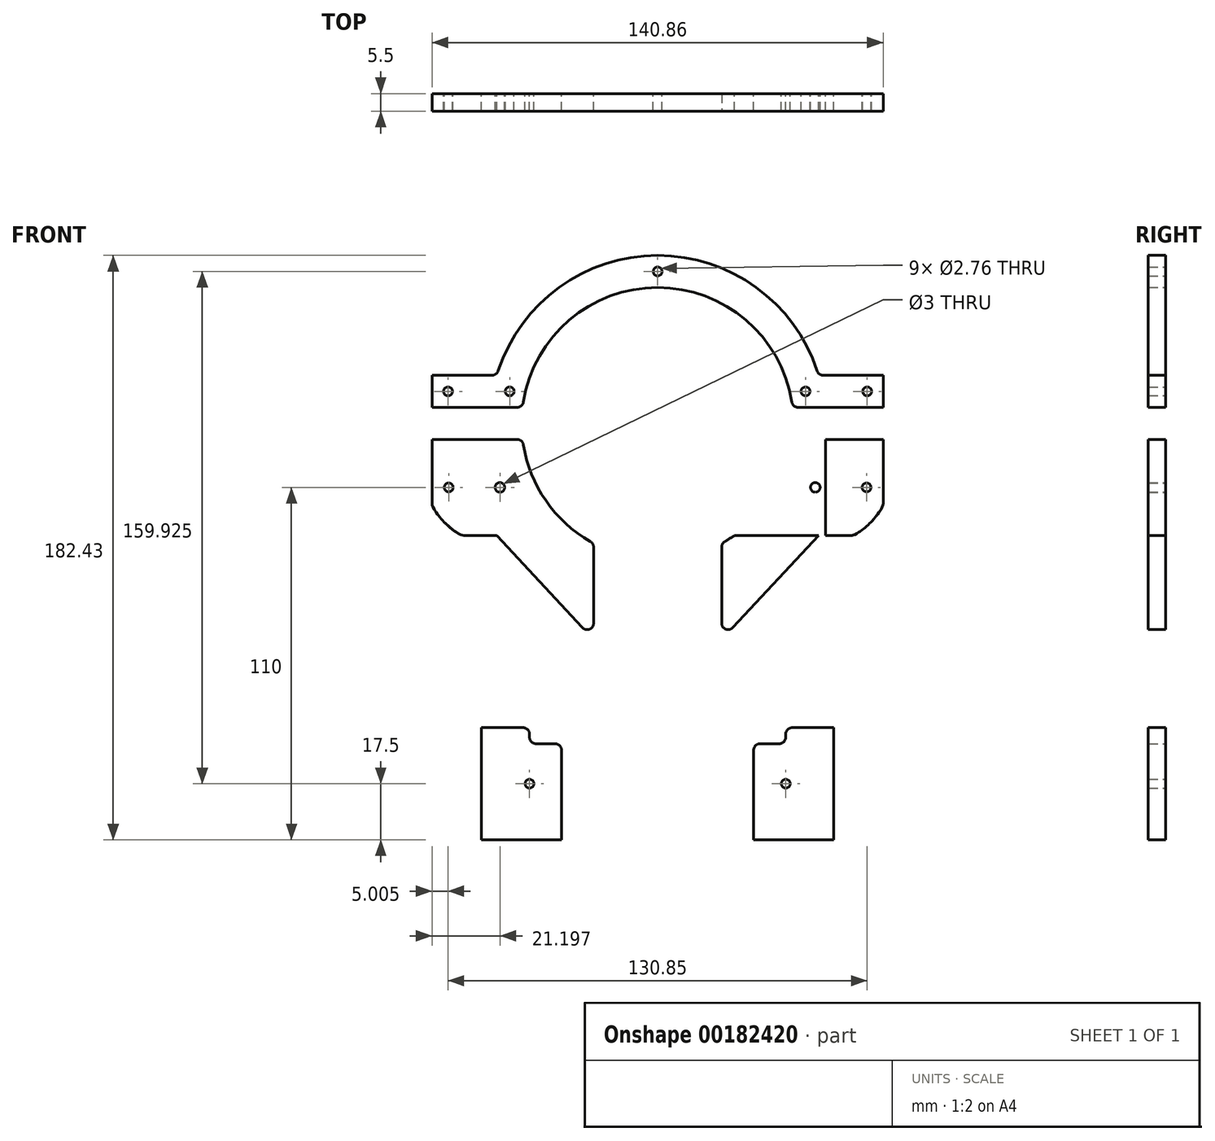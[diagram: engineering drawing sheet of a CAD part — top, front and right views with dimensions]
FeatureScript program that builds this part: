
annotation { "Feature Type Name" : "Feature", "Feature Type Description" : "" }
export const myFeature = defineFeature(function(context is Context, id is Id, definition is map)
    precondition{}
    {
        {
            var Q0;
            Q0=qCreatedBy(makeId("Front.planeOp"),FACE);
            var sketch = newSketch(context, id + "F0", { "sketchPlane" : qUnion([Q0])});
            skLineSegment(sketch, "E0", {"start": v(-40, 0) * mm, "end": v(40, 0) * mm});
            skLineSegment(sketch, "E1", {"start": v(0, 0) * mm, "end": v(0, 130) * mm, "construction": true});
            skLineSegment(sketch, "E2.top", {"start": v(-40, 30) * mm, "end": v(40, 30) * mm});
            skLineSegment(sketch, "E2.left", {"start": v(-40, 0) * mm, "end": v(-40, 30) * mm});
            skLineSegment(sketch, "E2.right", {"start": v(40, 0) * mm, "end": v(40, 30) * mm});
            skLineSegment(sketch, "E3.bottom", {"start": v(-20, 95) * mm, "end": v(20, 95) * mm});
            skLineSegment(sketch, "E3.top", {"start": v(-20, 30) * mm, "end": v(20, 30) * mm});
            skLineSegment(sketch, "E3.left", {"start": v(20, 95) * mm, "end": v(20, 30) * mm});
            skLineSegment(sketch, "E3.right", {"start": v(-20, 95) * mm, "end": v(-20, 30) * mm});
            skLineSegment(sketch, "E4", {"start": v(-30, 30) * mm, "end": v(-30, 0) * mm});
            skLineSegment(sketch, "E5.MirrorCS", {"start": v(30, 30) * mm, "end": v(30, 0) * mm});
            skPoint(sketch, "E6", {"position": v(0, 30) * mm});
            skLineSegment(sketch, "E7.bottom", {"start": v(-60.43, 130) * mm, "end": v(60.42, 130) * mm, "construction": true});
            skLineSegment(sketch, "E7.top", {"start": v(-60.43, 95) * mm, "end": v(60.43, 95) * mm});
            skLineSegment(sketch, "E7.left", {"start": v(-60.43, 125) * mm, "end": v(-60.43, 95) * mm});
            skLineSegment(sketch, "E7.right", {"start": v(60.42, 130) * mm, "end": v(60.42, 95) * mm});
            skPoint(sketch, "E8", {"position": v(0, 95) * mm});
            skCircle(sketch, "E9", {"center": v(0, 130) * mm, "radius": 40.42 * mm, "construction": true});
            skArc(sketch, "E10", {"start": v(-42.42, 130) * mm, "mid": v(0, 87.58) * mm, "end": v(42.42, 130) * mm});
            skLineSegment(sketch, "E11", {"start": v(-57.23, 130) * mm, "end": v(-57.23, 95) * mm});
            skLineSegment(sketch, "E12", {"start": v(-60.43, 125) * mm, "end": v(60.43, 125) * mm});
            skLineSegment(sketch, "E13.MirrorCS", {"start": v(57.23, 130) * mm, "end": v(57.23, 95) * mm});
            skLineSegment(sketch, "E14", {"start": v(-60.43, 135) * mm, "end": v(-40.11, 135) * mm});
            skLineSegment(sketch, "E15.trimOffspring", {"start": v(40.11, 135) * mm, "end": v(60.43, 135) * mm});
            skArc(sketch, "E16.trimOffspring", {"start": v(42.13, 135) * mm, "mid": v(0, 172.42) * mm, "end": v(-42.13, 135) * mm});
            skArc(sketch, "E17.0", {"start": v(50.23, 145) * mm, "mid": v(0, 182.43) * mm, "end": v(-50.23, 145) * mm});
            skLineSegment(sketch, "E18", {"start": v(-60.43, 145) * mm, "end": v(-50.23, 145) * mm});
            skLineSegment(sketch, "E19.MirrorCS", {"start": v(60.43, 145) * mm, "end": v(50.23, 145) * mm});
            skLineSegment(sketch, "E20", {"start": v(-60.43, 145) * mm, "end": v(-60.43, 135) * mm, "construction": true});
            skLineSegment(sketch, "E21", {"start": v(60.42, 145) * mm, "end": v(60.42, 135) * mm});
            skPoint(sketch, "E22.orphan", {"position": v(-39.68, 145) * mm});
            skPoint(sketch, "E23.orphan", {"position": v(39.68, 145) * mm});
            skLineSegment(sketch, "E24", {"start": v(-57.23, 135) * mm, "end": v(-57.23, 145) * mm});
            skLineSegment(sketch, "E25.MirrorCS", {"start": v(57.23, 135) * mm, "end": v(57.23, 145) * mm});
            skLineSegment(sketch, "E26", {"start": v(0, 95) * mm, "end": v(0, 30) * mm, "construction": true});
            skCircle(sketch, "E27", {"center": v(0, 62.5) * mm, "radius": 1.5 * mm});
            skLineSegment(sketch, "E28", {"start": v(-60.43, 110) * mm, "end": v(60.43, 110) * mm, "construction": true});
            skCircle(sketch, "E29", {"center": v(-49.23, 110) * mm, "radius": 1.5 * mm});
            skCircle(sketch, "E30.MirrorC", {"center": v(49.23, 110) * mm, "radius": 1.5 * mm});
            skCircle(sketch, "E31", {"center": v(0, 130) * mm, "radius": 52.42 * mm, "construction": true});
            skLineSegment(sketch, "E32", {"start": v(-60.43, 105) * mm, "end": v(-52.42, 105) * mm});
            skLineSegment(sketch, "E33", {"start": v(-52.42, 130) * mm, "end": v(-52.42, 95) * mm});
            skPoint(sketch, "E34", {"position": v(-52.42, 130) * mm});
            skLineSegment(sketch, "E35.MirrorCS", {"start": v(52.42, 130) * mm, "end": v(52.42, 95) * mm});
            skLineSegment(sketch, "E36.MirrorCS", {"start": v(60.43, 105) * mm, "end": v(52.42, 105) * mm});
            skLineSegment(sketch, "E37.bottom", {"start": v(-60.43, 95) * mm, "end": v(-70.43, 95) * mm});
            skLineSegment(sketch, "E37.top", {"start": v(-60.43, 145) * mm, "end": v(-70.43, 145) * mm});
            skLineSegment(sketch, "E37.left", {"start": v(-60.43, 95) * mm, "end": v(-60.43, 125) * mm, "construction": true});
            skLineSegment(sketch, "E37.right", {"start": v(-70.43, 95) * mm, "end": v(-70.43, 125) * mm});
            skLineSegment(sketch, "E38.trimOffspring", {"start": v(-60.43, 135) * mm, "end": v(-60.43, 145) * mm});
            skLineSegment(sketch, "E39", {"start": v(-60.43, 135) * mm, "end": v(-70.43, 135) * mm});
            skLineSegment(sketch, "E40", {"start": v(-60.43, 125) * mm, "end": v(-70.43, 125) * mm});
            skLineSegment(sketch, "E41.top", {"start": v(-60.43, 150) * mm, "end": v(-70.43, 150) * mm});
            skLineSegment(sketch, "E41.left", {"start": v(-60.43, 145) * mm, "end": v(-60.43, 150) * mm});
            skLineSegment(sketch, "E41.right", {"start": v(-70.43, 145) * mm, "end": v(-70.43, 150) * mm});
            skLineSegment(sketch, "E42.MirrorCS", {"start": v(70.43, 95) * mm, "end": v(70.43, 125) * mm});
            skLineSegment(sketch, "E43.MirrorCS", {"start": v(60.43, 125) * mm, "end": v(70.43, 125) * mm});
            skLineSegment(sketch, "E44.MirrorCS", {"start": v(60.43, 95) * mm, "end": v(70.43, 95) * mm});
            skLineSegment(sketch, "E45.MirrorCS", {"start": v(60.43, 135) * mm, "end": v(70.43, 135) * mm});
            skLineSegment(sketch, "E46.MirrorCS", {"start": v(70.43, 95) * mm, "end": v(70.43, 145) * mm});
            skLineSegment(sketch, "E47.MirrorCS", {"start": v(70.43, 145) * mm, "end": v(70.43, 150) * mm});
            skLineSegment(sketch, "E48.MirrorCS", {"start": v(60.43, 150) * mm, "end": v(70.43, 150) * mm});
            skLineSegment(sketch, "E49.MirrorCS", {"start": v(60.42, 145) * mm, "end": v(60.42, 150) * mm});
            skLineSegment(sketch, "E50.trimOffspring", {"start": v(-70.43, 135) * mm, "end": v(-70.43, 145) * mm});
            skLineSegment(sketch, "E51.trimOffspring", {"start": v(70.43, 135) * mm, "end": v(70.43, 145) * mm});
            skLineSegment(sketch, "E52", {"start": v(-70.43, 140) * mm, "end": v(70.43, 140) * mm, "construction": true});
            skLineSegment(sketch, "E53", {"start": v(-65.43, 145) * mm, "end": v(-65.43, 135) * mm, "construction": true});
            skCircle(sketch, "E54", {"center": v(-65.43, 140) * mm, "radius": 1.38 * mm});
            skLineSegment(sketch, "E55.bottom", {"start": v(-50.23, 145) * mm, "end": v(-42.13, 145) * mm, "construction": true});
            skLineSegment(sketch, "E55.top", {"start": v(-50.23, 135) * mm, "end": v(-42.13, 135) * mm, "construction": true});
            skLineSegment(sketch, "E55.left", {"start": v(-50.23, 145) * mm, "end": v(-50.23, 135) * mm, "construction": true});
            skLineSegment(sketch, "E55.right", {"start": v(-42.13, 145) * mm, "end": v(-42.13, 135) * mm, "construction": true});
            skLineSegment(sketch, "E56", {"start": v(-46.18, 145) * mm, "end": v(-46.18, 135) * mm, "construction": true});
            skCircle(sketch, "E57", {"center": v(-46.18, 140) * mm, "radius": 1.38 * mm});
            skCircle(sketch, "E58.MirrorC", {"center": v(46.18, 140) * mm, "radius": 1.38 * mm});
            skCircle(sketch, "E59.MirrorC", {"center": v(65.43, 140) * mm, "radius": 1.38 * mm});
            skLineSegment(sketch, "E60.bottom", {"start": v(-40, 0) * mm, "end": v(-55, 0) * mm});
            skLineSegment(sketch, "E60.top", {"start": v(-40, 35) * mm, "end": v(-55, 35) * mm});
            skLineSegment(sketch, "E60.left", {"start": v(-40, 0) * mm, "end": v(-40, 35) * mm});
            skLineSegment(sketch, "E60.right", {"start": v(-55, 0) * mm, "end": v(-55, 35) * mm});
            skLineSegment(sketch, "E61.MirrorCS", {"start": v(40, 35) * mm, "end": v(55, 35) * mm});
            skLineSegment(sketch, "E62.MirrorCS", {"start": v(40, 0) * mm, "end": v(40, 35) * mm});
            skLineSegment(sketch, "E63.MirrorCS", {"start": v(55, 0) * mm, "end": v(55, 35) * mm});
            skLineSegment(sketch, "E64.MirrorCS", {"start": v(40, 0) * mm, "end": v(55, 0) * mm});
            skLineSegment(sketch, "E65", {"start": v(-55, 17.5) * mm, "end": v(55, 17.5) * mm, "construction": true});
            skCircle(sketch, "E66", {"center": v(-40, 17.5) * mm, "radius": 1.38 * mm});
            skCircle(sketch, "E67", {"center": v(-20, 17.5) * mm, "radius": 1.38 * mm});
            skCircle(sketch, "E68.MirrorC", {"center": v(20, 17.5) * mm, "radius": 1.38 * mm});
            skCircle(sketch, "E69.MirrorC", {"center": v(40, 17.5) * mm, "radius": 1.38 * mm});
            skCircle(sketch, "E70", {"center": v(-65.23, 110) * mm, "radius": 1.38 * mm});
            skCircle(sketch, "E71.MirrorC", {"center": v(65.23, 110) * mm, "radius": 1.38 * mm});
            skLineSegment(sketch, "E72", {"start": v(-50.23, 95) * mm, "end": v(-50.23, 135) * mm, "construction": true});
            skLineSegment(sketch, "E73", {"start": v(-50.23, 95) * mm, "end": v(-20, 62.5) * mm});
            skLineSegment(sketch, "E74.MirrorCS", {"start": v(50.23, 95) * mm, "end": v(20, 62.5) * mm});
            skLineSegment(sketch, "E75", {"start": v(0, 182.43) * mm, "end": v(0, 172.42) * mm, "construction": true});
            skCircle(sketch, "E76", {"center": v(0, 177.43) * mm, "radius": 1.38 * mm});
            skLineSegment(sketch, "E77", {"start": v(70.43, 145) * mm, "end": v(60.43, 145) * mm});
            skSolve(sketch);
        }
        {
            var Q0;
            {var subQ0=sQuery(id+"F0.wireOp",EDGE,"E12");var subQ5=sQuery(id+"F0.wireOp",EDGE,"E11");var subQ6=makeQuery(id+"F0.imprint","INTERSECT",VERTEX,{"derivedFrom":[subQ5,subQ0]});Q0=makeQuery(id+"F0.imprint","IMPRINT",FACE,{"disambiguationData":[TD([[makeQuery(id+"F0.imprint","IMPRINT",EDGE,{"disambiguationData":[TD([[subQ6,-1.0]])],"derivedFrom":subQ5}),-1.0]])]});}
            var Q1;
            Q1=makeQuery(id+"F0.imprint","IMPRINT",FACE,{"disambiguationData":[TD([[makeQuery(id+"F0.imprint","IMPRINT",EDGE,{"derivedFrom":sQuery(id+"F0.wireOp",EDGE,"E29")}),-1.0]])]});
            var Q2;
            {var subQ0=sQuery(id+"F0.wireOp",EDGE,"E12");var subQ5=sQuery(id+"F0.wireOp",EDGE,"E13.MirrorCS");var subQ6=makeQuery(id+"F0.imprint","INTERSECT",VERTEX,{"derivedFrom":[subQ0,subQ5]});Q2=makeQuery(id+"F0.imprint","IMPRINT",FACE,{"disambiguationData":[TD([[makeQuery(id+"F0.imprint","IMPRINT",EDGE,{"disambiguationData":[TD([[subQ6,-1.0]])],"derivedFrom":subQ5}),1.0]])]});}
            var Q3;
            {var subQ0=sQuery(id+"F0.wireOp",EDGE,"E35.MirrorCS");var subQ1=sQuery(id+"F0.wireOp",EDGE,"E12");var subQ2=makeQuery(id+"F0.imprint","INTERSECT",VERTEX,{"derivedFrom":[subQ1,subQ0]});Q3=makeQuery(id+"F0.imprint","IMPRINT",FACE,{"disambiguationData":[TD([[makeQuery(id+"F0.imprint","IMPRINT",EDGE,{"disambiguationData":[TD([[subQ2,-1.0]])],"derivedFrom":subQ1}),-1.0]])]});}
            var Q4;
            {var subQ0=sQuery(id+"F0.wireOp",EDGE,"E16.trimOffspring");Q4=makeQuery(id+"F0.imprint","IMPRINT",FACE,{"disambiguationData":[TD([[makeQuery(id+"F0.imprint","IMPRINT",EDGE,{"derivedFrom":subQ0}),-1.0]])]});}
            var Q5;
            {var subQ0=sQuery(id+"F0.wireOp",EDGE,"E21");Q5=makeQuery(id+"F0.imprint","IMPRINT",FACE,{"disambiguationData":[TD([[makeQuery(id+"F0.imprint","IMPRINT",EDGE,{"derivedFrom":subQ0}),-1.0]])]});}
            var Q6;
            {var subQ5=sQuery(id+"F0.wireOp",EDGE,"E3.top");Q6=makeQuery(id+"F0.imprint","IMPRINT",FACE,{"disambiguationData":[TD([[makeQuery(id+"F0.imprint","IMPRINT",EDGE,{"derivedFrom":subQ5}),1.0]])]});}
            var Q7;
            {var subQ0=sQuery(id+"F0.wireOp",EDGE,"E3.top");Q7=makeQuery(id+"F0.imprint","IMPRINT",FACE,{"disambiguationData":[TD([[makeQuery(id+"F0.imprint","IMPRINT",EDGE,{"derivedFrom":subQ0}),-1.0]])]});}
            var Q8;
            {var subQ2=sQuery(id+"F0.wireOp",EDGE,"E24");Q8=makeQuery(id+"F0.imprint","IMPRINT",FACE,{"disambiguationData":[TD([[makeQuery(id+"F0.imprint","IMPRINT",EDGE,{"derivedFrom":subQ2}),1.0]])]});}
            var Q9;
            Q9=makeQuery(id+"F0.imprint","IMPRINT",FACE,{"disambiguationData":[TD([[makeQuery(id+"F0.imprint","IMPRINT",EDGE,{"derivedFrom":sQuery(id+"F0.wireOp",EDGE,"E38.trimOffspring")}),1.0]])]});
            var Q10;
            {var subQ0=sQuery(id+"F0.wireOp",EDGE,"E37.bottom");Q10=makeQuery(id+"F0.imprint","IMPRINT",FACE,{"disambiguationData":[TD([[makeQuery(id+"F0.imprint","IMPRINT",EDGE,{"derivedFrom":subQ0}),-1.0]])]});}
            var Q11;
            {var subQ1=sQuery(id+"F0.wireOp",EDGE,"E7.top");var subQ3=sQuery(id+"F0.wireOp",EDGE,"E11");var subQ4=makeQuery(id+"F0.imprint","INTERSECT",VERTEX,{"derivedFrom":[subQ1,subQ3]});Q11=makeQuery(id+"F0.imprint","IMPRINT",FACE,{"disambiguationData":[TD([[makeQuery(id+"F0.imprint","IMPRINT",EDGE,{"disambiguationData":[TD([[subQ4,1.0]])],"derivedFrom":subQ3}),-1.0]])]});}
            var Q12;
            {var subQ0=sQuery(id+"F0.wireOp",EDGE,"E11");var subQ1=sQuery(id+"F0.wireOp",EDGE,"E7.top");var subQ2=makeQuery(id+"F0.imprint","INTERSECT",VERTEX,{"derivedFrom":[subQ1,subQ0]});Q12=makeQuery(id+"F0.imprint","IMPRINT",FACE,{"disambiguationData":[TD([[makeQuery(id+"F0.imprint","IMPRINT",EDGE,{"disambiguationData":[TD([[subQ2,-1.0]])],"derivedFrom":subQ1}),1.0]])]});}
            var Q13;
            {var subQ0=sQuery(id+"F0.wireOp",EDGE,"E13.MirrorCS");var subQ1=sQuery(id+"F0.wireOp",EDGE,"E7.top");var subQ2=makeQuery(id+"F0.imprint","INTERSECT",VERTEX,{"derivedFrom":[subQ1,subQ0]});Q13=makeQuery(id+"F0.imprint","IMPRINT",FACE,{"disambiguationData":[TD([[makeQuery(id+"F0.imprint","IMPRINT",EDGE,{"disambiguationData":[TD([[subQ2,1.0]])],"derivedFrom":subQ1}),1.0]])]});}
            var Q14;
            {var subQ1=sQuery(id+"F0.wireOp",EDGE,"E7.top");var subQ3=sQuery(id+"F0.wireOp",EDGE,"E13.MirrorCS");var subQ4=makeQuery(id+"F0.imprint","INTERSECT",VERTEX,{"derivedFrom":[subQ1,subQ3]});Q14=makeQuery(id+"F0.imprint","IMPRINT",FACE,{"disambiguationData":[TD([[makeQuery(id+"F0.imprint","IMPRINT",EDGE,{"disambiguationData":[TD([[subQ4,1.0]])],"derivedFrom":subQ3}),1.0]])]});}
            var Q15;
            {var subQ1=sQuery(id+"F0.wireOp",EDGE,"E43.MirrorCS");Q15=makeQuery(id+"F0.imprint","IMPRINT",FACE,{"disambiguationData":[TD([[makeQuery(id+"F0.imprint","IMPRINT",EDGE,{"derivedFrom":subQ1}),-1.0]])]});}
            var Q16;
            Q16=makeQuery(id+"F0.imprint","IMPRINT",FACE,{"disambiguationData":[TD([[makeQuery(id+"F0.imprint","IMPRINT",EDGE,{"derivedFrom":sQuery(id+"F0.wireOp",EDGE,"E21")}),1.0]])]});
            var Q17;
            {var subQ5=sQuery(id+"F0.wireOp",EDGE,"E4");Q17=makeQuery(id+"F0.imprint","IMPRINT",FACE,{"disambiguationData":[TD([[makeQuery(id+"F0.imprint","IMPRINT",EDGE,{"derivedFrom":subQ5}),-1.0]])]});}
            var Q18;
            {var subQ5=sQuery(id+"F0.wireOp",EDGE,"E60.bottom");Q18=makeQuery(id+"F0.imprint","IMPRINT",FACE,{"disambiguationData":[TD([[makeQuery(id+"F0.imprint","IMPRINT",EDGE,{"derivedFrom":subQ5}),-1.0]])]});}
            var Q19;
            {var subQ2=sQuery(id+"F0.wireOp",EDGE,"E61.MirrorCS");Q19=makeQuery(id+"F0.imprint","IMPRINT",FACE,{"disambiguationData":[TD([[makeQuery(id+"F0.imprint","IMPRINT",EDGE,{"derivedFrom":subQ2}),-1.0]])]});}
            var Q20;
            {var subQ0=sQuery(id+"F0.wireOp",EDGE,"E5.MirrorCS");Q20=makeQuery(id+"F0.imprint","IMPRINT",FACE,{"disambiguationData":[TD([[makeQuery(id+"F0.imprint","IMPRINT",EDGE,{"derivedFrom":subQ0}),1.0]])]});}
            var Q21;
            {var subQ0=sQuery(id+"F0.wireOp",EDGE,"E74.MirrorCS");Q21=makeQuery(id+"F0.imprint","IMPRINT",FACE,{"disambiguationData":[TD([[makeQuery(id+"F0.imprint","IMPRINT",EDGE,{"derivedFrom":subQ0}),-1.0]])]});}
            var Q22;
            {var subQ0=sQuery(id+"F0.wireOp",EDGE,"E73");Q22=makeQuery(id+"F0.imprint","IMPRINT",FACE,{"disambiguationData":[TD([[makeQuery(id+"F0.imprint","IMPRINT",EDGE,{"derivedFrom":subQ0}),1.0]])]});}
            var Q23;
            Q23=makeQuery(id+"F0.imprint","IMPRINT",FACE,{"disambiguationData":[TD([[makeQuery(id+"F0.imprint","IMPRINT",EDGE,{"derivedFrom":sQuery(id+"F0.wireOp",EDGE,"E30.MirrorC")}),1.0]])]});
            var Q24;
            {var subQ0=sQuery(id+"F0.wireOp",EDGE,"E12");var subQ1=sQuery(id+"F0.wireOp",EDGE,"E11");var subQ2=makeQuery(id+"F0.imprint","INTERSECT",VERTEX,{"derivedFrom":[subQ1,subQ0]});Q24=makeQuery(id+"F0.imprint","IMPRINT",FACE,{"disambiguationData":[TD([[makeQuery(id+"F0.imprint","IMPRINT",EDGE,{"disambiguationData":[TD([[subQ2,-1.0]])],"derivedFrom":subQ1}),1.0]])]});}
            extrude(context, id + "F1", {"entities" : qUnion([Q0, Q1, Q2, Q3, Q4, Q5, Q6, Q7, Q8, Q9, Q10, Q11, Q12, Q13, Q14, Q15, Q16, Q17, Q18, Q19, Q20, Q21, Q22, Q23, Q24]), "depth" : 5.5 * mm});
        }
        {
            var Q0;
            Q0=makeQuery(id+"F1.opExtrude","SWEPT_EDGE",EDGE,{"disambiguationData":[OSD([sQuery(id+"F0.wireOp",EDGE,"E17.0"),sQuery(id+"F0.wireOp",EDGE,"E18")])]});
            var Q1;
            Q1=makeQuery(id+"F1.opExtrude","SWEPT_EDGE",EDGE,{"disambiguationData":[OSD([sQuery(id+"F0.wireOp",EDGE,"E18"),sQuery(id+"F0.wireOp",EDGE,"E38.trimOffspring"),sQuery(id+"F0.wireOp",EDGE,"E37.top"),sQuery(id+"F0.wireOp",EDGE,"E41.left")])]});
            var Q2;
            Q2=makeQuery(id+"F1.opExtrude","SWEPT_EDGE",EDGE,{"disambiguationData":[OSD([sQuery(id+"F0.wireOp",EDGE,"E41.top"),sQuery(id+"F0.wireOp",EDGE,"E41.left")])]});
            var Q3;
            Q3=makeQuery(id+"F1.opExtrude","SWEPT_EDGE",EDGE,{"disambiguationData":[OSD([sQuery(id+"F0.wireOp",EDGE,"E17.0"),sQuery(id+"F0.wireOp",EDGE,"E19.MirrorCS")])]});
            var Q4;
            Q4=makeQuery(id+"F1.opExtrude","SWEPT_EDGE",EDGE,{"disambiguationData":[OSD([sQuery(id+"F0.wireOp",EDGE,"E19.MirrorCS"),sQuery(id+"F0.wireOp",EDGE,"E21"),sQuery(id+"F0.wireOp",EDGE,"E49.MirrorCS")])]});
            var Q5;
            Q5=makeQuery(id+"F1.opExtrude","SWEPT_EDGE",EDGE,{"disambiguationData":[OSD([sQuery(id+"F0.wireOp",EDGE,"E49.MirrorCS"),sQuery(id+"F0.wireOp",EDGE,"E48.MirrorCS")])]});
            var Q6;
            Q6=makeQuery(id+"F1.opExtrude","SWEPT_EDGE",EDGE,{"disambiguationData":[OSD([sQuery(id+"F0.wireOp",EDGE,"E2.top"),sQuery(id+"F0.wireOp",EDGE,"E60.left")])]});
            var Q7;
            Q7=makeQuery(id+"F1.opExtrude","SWEPT_EDGE",EDGE,{"disambiguationData":[OSD([sQuery(id+"F0.wireOp",EDGE,"E60.top"),sQuery(id+"F0.wireOp",EDGE,"E60.left")])]});
            var Q8;
            Q8=makeQuery(id+"F1.opExtrude","SWEPT_EDGE",EDGE,{"disambiguationData":[OSD([sQuery(id+"F0.wireOp",EDGE,"E2.top"),sQuery(id+"F0.wireOp",EDGE,"E3.top"),sQuery(id+"F0.wireOp",EDGE,"E3.right")])]});
            var Q9;
            Q9=makeQuery(id+"F1.opExtrude","SWEPT_EDGE",EDGE,{"disambiguationData":[OSD([sQuery(id+"F0.wireOp",EDGE,"E2.top"),sQuery(id+"F0.wireOp",EDGE,"E3.top"),sQuery(id+"F0.wireOp",EDGE,"E3.left")])]});
            var Q10;
            Q10=makeQuery(id+"F1.opExtrude","SWEPT_EDGE",EDGE,{"disambiguationData":[OSD([sQuery(id+"F0.wireOp",EDGE,"E2.top"),sQuery(id+"F0.wireOp",EDGE,"E62.MirrorCS")])]});
            var Q11;
            Q11=makeQuery(id+"F1.opExtrude","SWEPT_EDGE",EDGE,{"disambiguationData":[OSD([sQuery(id+"F0.wireOp",EDGE,"E61.MirrorCS"),sQuery(id+"F0.wireOp",EDGE,"E62.MirrorCS")])]});
            var Q12;
            {var subQ0=sQuery(id+"F0.wireOp",EDGE,"E10");var subQ1=sQuery(id+"F0.wireOp",EDGE,"E12");Q12=makeQuery(id+"F1.opExtrude","SWEPT_EDGE",EDGE,{"disambiguationData":[OSD([subQ1,subQ0]),TDD([makeQuery(id+"F0.imprint","INTERSECT",VERTEX,{"disambiguationData":[OD(0.0)],"derivedFrom":[subQ1,subQ0]})])]});}
            var Q13;
            {var subQ0=sQuery(id+"F0.wireOp",EDGE,"E10");var subQ1=sQuery(id+"F0.wireOp",EDGE,"E12");Q13=makeQuery(id+"F1.opExtrude","SWEPT_EDGE",EDGE,{"disambiguationData":[OSD([subQ1,subQ0]),TDD([makeQuery(id+"F0.imprint","INTERSECT",VERTEX,{"disambiguationData":[OD(1.0)],"derivedFrom":[subQ1,subQ0]})])]});}
            var Q14;
            Q14=makeQuery(id+"F1.opExtrude","SWEPT_EDGE",EDGE,{"disambiguationData":[OSD([sQuery(id+"F0.wireOp",EDGE,"E14"),sQuery(id+"F0.wireOp",EDGE,"E16.trimOffspring")])]});
            var Q15;
            Q15=makeQuery(id+"F1.opExtrude","SWEPT_EDGE",EDGE,{"disambiguationData":[OSD([sQuery(id+"F0.wireOp",EDGE,"E15.trimOffspring"),sQuery(id+"F0.wireOp",EDGE,"E16.trimOffspring")])]});
            var Q16;
            Q16=makeQuery(id+"F1.opExtrude","SWEPT_EDGE",EDGE,{"disambiguationData":[OSD([sQuery(id+"F0.wireOp",EDGE,"E3.right"),sQuery(id+"F0.wireOp",EDGE,"E73")])]});
            var Q17;
            Q17=makeQuery(id+"F1.opExtrude","SWEPT_EDGE",EDGE,{"disambiguationData":[OSD([sQuery(id+"F0.wireOp",EDGE,"E3.left"),sQuery(id+"F0.wireOp",EDGE,"E74.MirrorCS")])]});
            fillet(context, id + "F2", {"entities" : qUnion([Q0, Q1, Q2, Q3, Q4, Q5, Q6, Q7, Q8, Q9, Q10, Q11, Q12, Q13, Q14, Q15, Q16, Q17]), "radius" : 2 * mm, "tangentPropagation" : true, "allowEdgeOverflow" : false});
        }
        {
            var Q0;
            Q0=makeQuery(id+"F1.opExtrude","SWEPT_EDGE",EDGE,{"disambiguationData":[OSD([sQuery(id+"F0.wireOp",EDGE,"E37.bottom"),sQuery(id+"F0.wireOp",EDGE,"E37.right")])]});
            var Q1;
            Q1=makeQuery(id+"F1.opExtrude","SWEPT_EDGE",EDGE,{"disambiguationData":[OSD([sQuery(id+"F0.wireOp",EDGE,"E44.MirrorCS"),sQuery(id+"F0.wireOp",EDGE,"E42.MirrorCS")])]});
            fillet(context, id + "F3", {"entities" : qUnion([Q0, Q1]), "radius" : 10 * mm, "tangentPropagation" : true, "rho" : .2, "crossSection" : FilletCrossSection.CONIC, "allowEdgeOverflow" : false});
        }
    });
